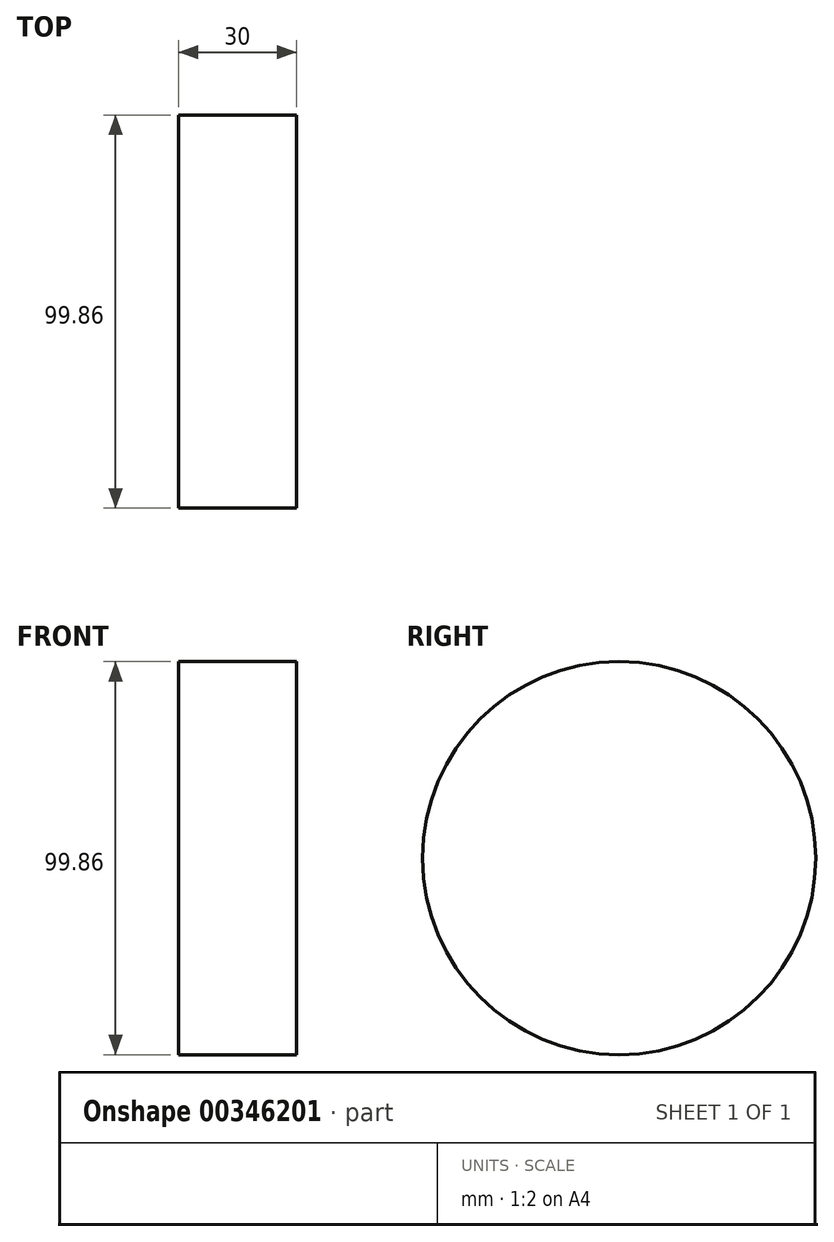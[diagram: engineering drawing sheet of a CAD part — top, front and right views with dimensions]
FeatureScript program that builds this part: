
annotation { "Feature Type Name" : "Feature", "Feature Type Description" : "" }
export const myFeature = defineFeature(function(context is Context, id is Id, definition is map)
    precondition{}
    {
        {
            var Q0;
            Q0=qCreatedBy(makeId("Right.planeOp"),FACE);
            var sketch = newSketch(context, id + "F0", { "sketchPlane" : qUnion([Q0])});
            skCircle(sketch, "E0", {"center": v(0, 0) * mm, "radius": 49.93 * mm});
            skSolve(sketch);
        }
        {
            var Q0;
            Q0=makeQuery(id+"F0.imprint","IMPRINT",FACE,{"disambiguationData":[TD([[makeQuery(id+"F0.imprint","IMPRINT",EDGE,{"derivedFrom":sQuery(id+"F0.wireOp",EDGE,"E0")}),1.0]])]});
            extrude(context, id + "F1", {"entities" : qUnion([Q0]), "depth" : 30 * mm});
        }
    });
